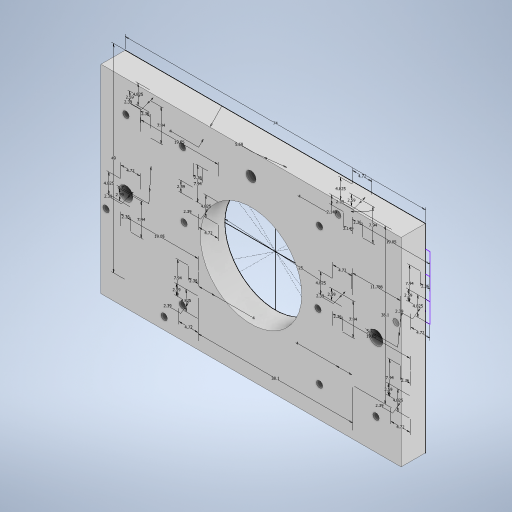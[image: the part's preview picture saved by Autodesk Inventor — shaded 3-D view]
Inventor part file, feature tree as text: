
AUTODESK INVENTOR PART (.ipt)
format: ipt  version: 2024 (Build 280153000, 153)  size: 338,944 bytes
history: native  units: in
note: dims shown in document units (in); Inventor stores cm internally (conversion verified against a paired STEP export)
features: hole x4, sketch x1, extrude x1
ambient origin geometry x8: Origin, YZ Plane, XZ Plane, XY Plane, X Axis, Y Axis, Z Axis, Center Point
bodies: Solid1 (feature_tree)
feature tree (6):
  sketch  "Sketch1"  dims[d0=2.9134in d1=1.9291in d2=0.9843in d3=1.5in d4=1.5in d5=0.0846in d6=0.0846in d7=0.464in d8=0.2362in d9=0.0in d10=0.0617in d11=0.1575in d12=0.375in d13=0.25in d14=0.5635in d15=0.1969in d16=0.0in d17=0.1339in d18=0.25in d19=0.375in d20=0.25in d21=0.5635in d22=0.328in d23=0.0in d24=0.1575in d25=0.1575in d26=0.1575in d27=0.1575in d28=0.2244in d29=0.2244in d30=0.75in d31=0.0929in d32=0.3126in d33=0.0929in d34=0.3126in d35=0.102in d36=0.102in d37=0.19in d39=0.19in d40=0.1858in d41=0.0941in d42=0.0941in d43=0.75in d44=0.0929in d45=0.3126in d46=0.0929in d47=0.3126in d48=0.102in d49=0.102in d50=0.19in d51=0.1858in d52=0.19in d53=0.1858in d54=0.0941in d55=0.0941in d56=0.75in d57=0.0929in d58=0.3126in d59=0.0929in d60=0.3126in d61=0.102in d62=0.102in d63=0.19in d64=0.1858in d65=0.19in d66=0.1858in d67=0.0941in d68=0.0941in d69=0.75in d70=0.0929in d71=0.3126in d72=0.0929in d73=0.3126in d74=0.102in d75=0.102in d76=0.19in d77=0.1858in d78=0.19in d79=0.1858in d80=0.0941in d81=0.0941in d82=0.0617in d83=0.1575in d84=0.1575in d85=0.0787in d86=90.0deg d87=0.315in d88=0.8108in d89=0.2236in d90=0.0968in d91=0.2362in d92=0.119in d93=0.0787in d94=0.5635in d95=0.315in d96=0.8108in]
  extrude  "Extrusion1"  Depth=1.9291in
  hole  "Hole1"  [1 undecoded]
  hole  "Hole2"  [1 undecoded]
  hole  "Hole3"  [1 undecoded]
  hole  "Hole4"  [1 undecoded]
note: 4 required parameter values undecoded (feature->parameter linkage not recoverable at this tier; creation-order binding heuristic only, values carry confidence <= 0.55)
